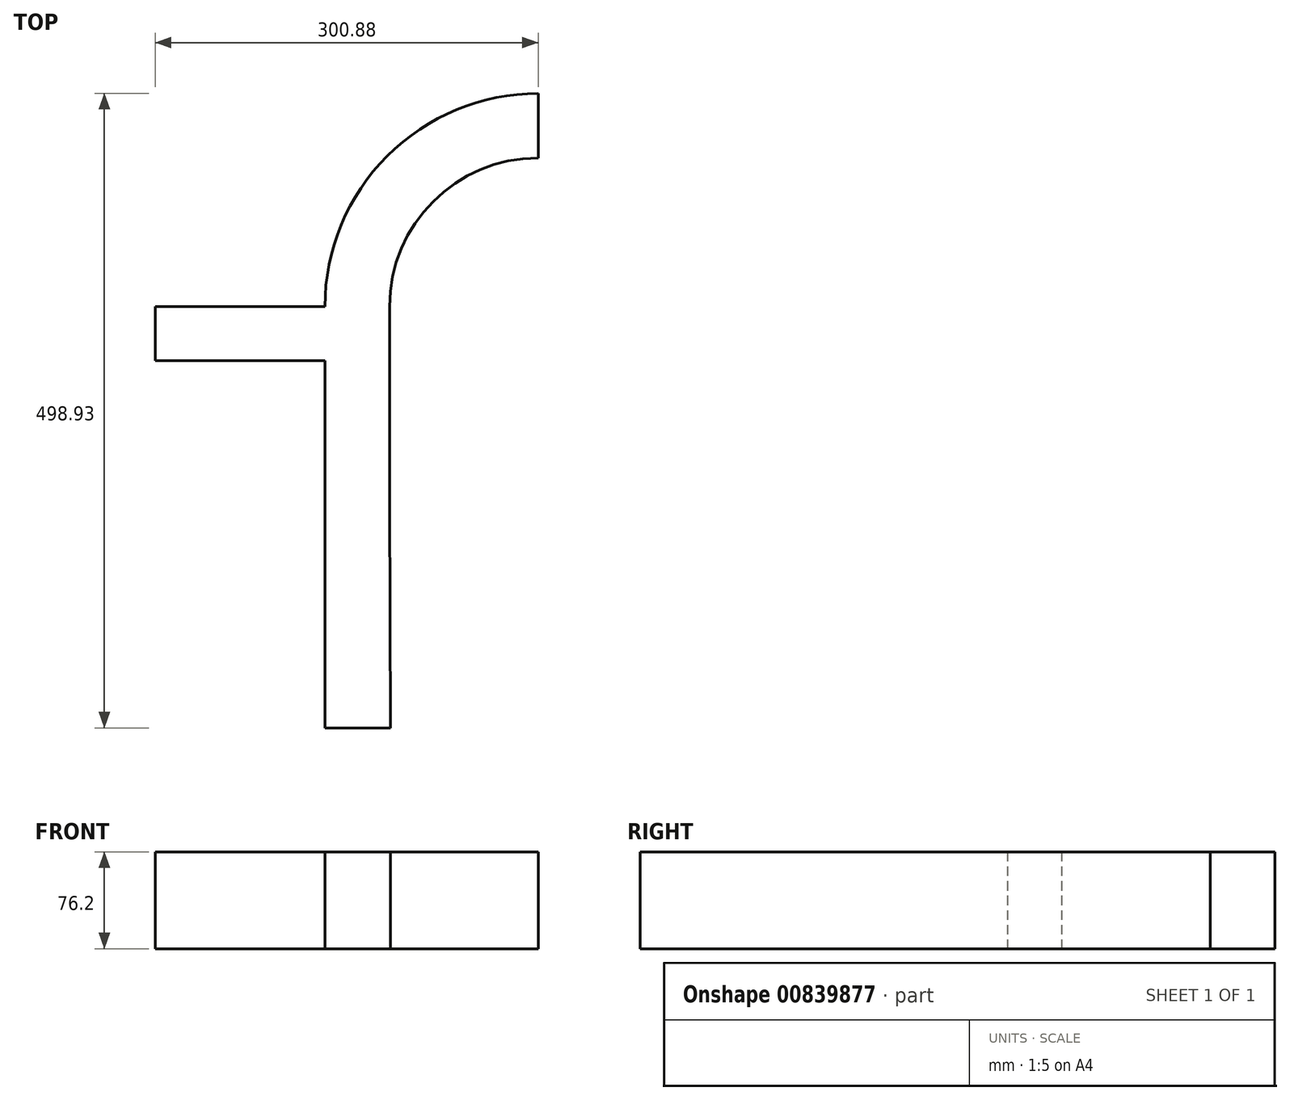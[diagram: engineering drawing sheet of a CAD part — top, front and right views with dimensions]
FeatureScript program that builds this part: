
annotation { "Feature Type Name" : "Feature", "Feature Type Description" : "" }
export const myFeature = defineFeature(function(context is Context, id is Id, definition is map)
    precondition{}
    {
        {
            var Q0;
            Q0=qCreatedBy(makeId("Top.planeOp"),FACE);
            var sketch = newSketch(context, id + "F0", { "sketchPlane" : qUnion([Q0])});
            skLineSegment(sketch, "E0.left", {"start": v(0, 0) * mm, "end": v(0, 109.73) * mm});
            skLineSegment(sketch, "E0.right", {"start": v(50.8, 0) * mm, "end": v(50.8, 152.4) * mm});
            skArc(sketch, "E1", {"start": v(167.54, 319.9) * mm, "mid": v(49.07, 270.85) * mm, "end": v(0, 152.4) * mm});
            skArc(sketch, "E2", {"start": v(167.54, 269.14) * mm, "mid": v(85, 234.95) * mm, "end": v(50.8, 152.4) * mm});
            skLineSegment(sketch, "E3", {"start": v(167.54, 269.14) * mm, "end": v(167.54, 319.9) * mm});
            skPoint(sketch, "E4.orphan", {"position": v(198.64, 264.92) * mm});
            skPoint(sketch, "E5.orphan", {"position": v(198.64, 316.97) * mm});
            skLineSegment(sketch, "E6", {"start": v(0, 152.4) * mm, "end": v(-133.34, 152.4) * mm});
            skLineSegment(sketch, "E7", {"start": v(-133.34, 152.4) * mm, "end": v(-133.34, 109.73) * mm});
            skLineSegment(sketch, "E8", {"start": v(-133.34, 109.73) * mm, "end": v(0, 109.73) * mm});
            skLineSegment(sketch, "E9", {"start": v(0, 0) * mm, "end": v(0, -179.03) * mm});
            skLineSegment(sketch, "E10", {"start": v(0, -179.03) * mm, "end": v(51.31, -179.03) * mm});
            skLineSegment(sketch, "E11", {"start": v(51.31, -179.03) * mm, "end": v(50.8, 0) * mm});
            skSolve(sketch);
        }
        {
            var Q0;
            Q0=makeQuery(id+"F0.imprint","IMPRINT",FACE,{"disambiguationData":[TD([[makeQuery(id+"F0.imprint","IMPRINT",EDGE,{"derivedFrom":sQuery(id+"F0.wireOp",EDGE,"E0.left")}),-1.0]])]});
            var Q1;
            Q1 = qConstructionFilter(qBodyType(qCreatedBy(id + "F0" ,EDGE), BodyType.WIRE), ConstructionObject.NO);
            extrude(context, id + "F1", {"entities" : qUnion([Q0]), "surfaceEntities" : qUnion([Q1]), "depth" : 76.2 * mm, "offsetDistance" : 25.4 * mm});
        }
    });
